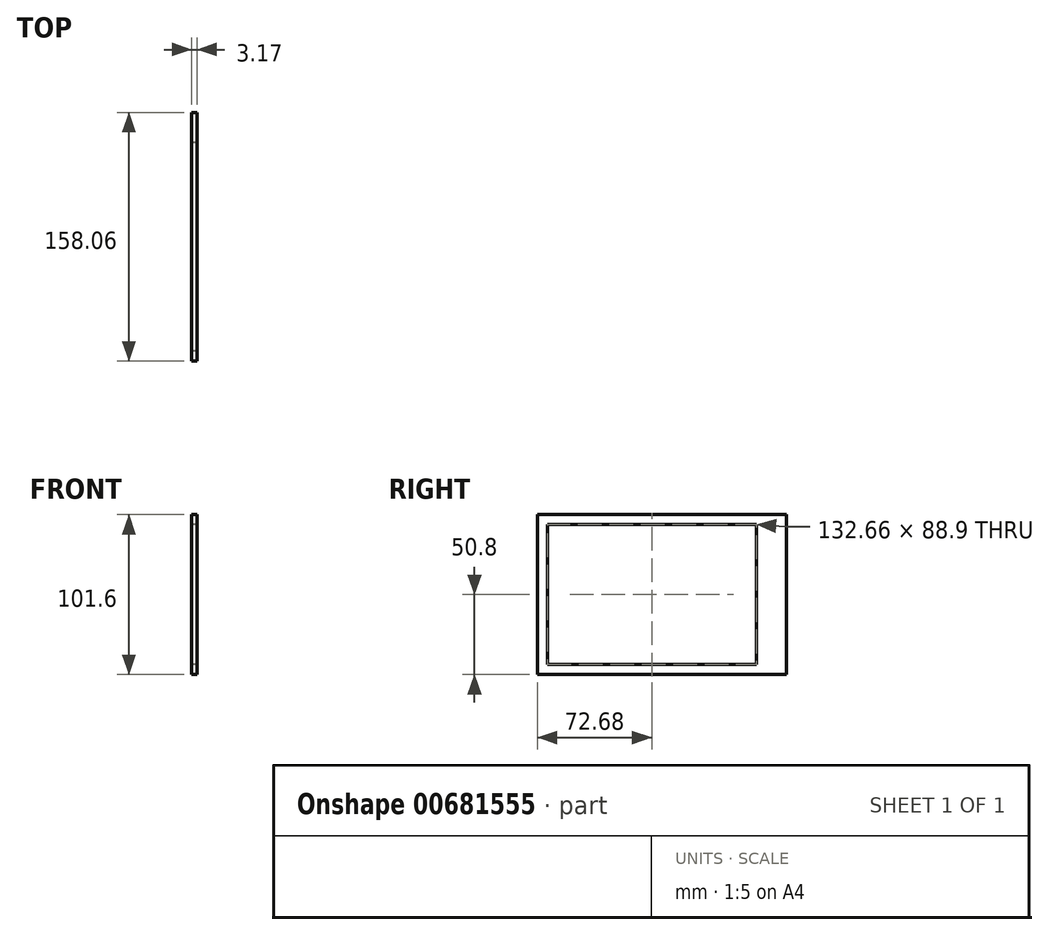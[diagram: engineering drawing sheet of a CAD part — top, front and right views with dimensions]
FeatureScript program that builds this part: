
annotation { "Feature Type Name" : "Feature", "Feature Type Description" : "" }
export const myFeature = defineFeature(function(context is Context, id is Id, definition is map)
    precondition{}
    {
        {
            var Q0;
            Q0=qCreatedBy(makeId("Right.planeOp"),FACE);
            var sketch = newSketch(context, id + "F0", { "sketchPlane" : qUnion([Q0])});
            skLineSegment(sketch, "E0.bottom", {"start": v(79.03, 50.8) * mm, "end": v(-79.03, 50.8) * mm});
            skLineSegment(sketch, "E0.top", {"start": v(79.03, -50.8) * mm, "end": v(-79.03, -50.8) * mm});
            skLineSegment(sketch, "E0.left", {"start": v(79.03, 50.8) * mm, "end": v(79.03, -50.8) * mm});
            skLineSegment(sketch, "E0.right", {"start": v(-79.03, 50.8) * mm, "end": v(-79.03, -50.8) * mm});
            skPoint(sketch, "E0.middle", {"position": v(0, 0) * mm});
            skLineSegment(sketch, "E1.bottom", {"start": v(72.68, 44.45) * mm, "end": v(-72.68, 44.45) * mm});
            skLineSegment(sketch, "E1.top", {"start": v(72.68, -44.45) * mm, "end": v(-72.68, -44.45) * mm});
            skLineSegment(sketch, "E2", {"start": v(-72.68, 44.45) * mm, "end": v(-72.68, -44.45) * mm});
            skLineSegment(sketch, "E3", {"start": v(59.98, 44.45) * mm, "end": v(59.98, -44.45) * mm});
            skSolve(sketch);
        }
        {
            var Q0;
            Q0 = qSketchRegion(id + "F0", true);
            extrude(context, id + "F1", {"entities" : qUnion([Q0]), "depth" : 3.17 * mm, "offsetDistance" : 25.4 * mm});
        }
    });
